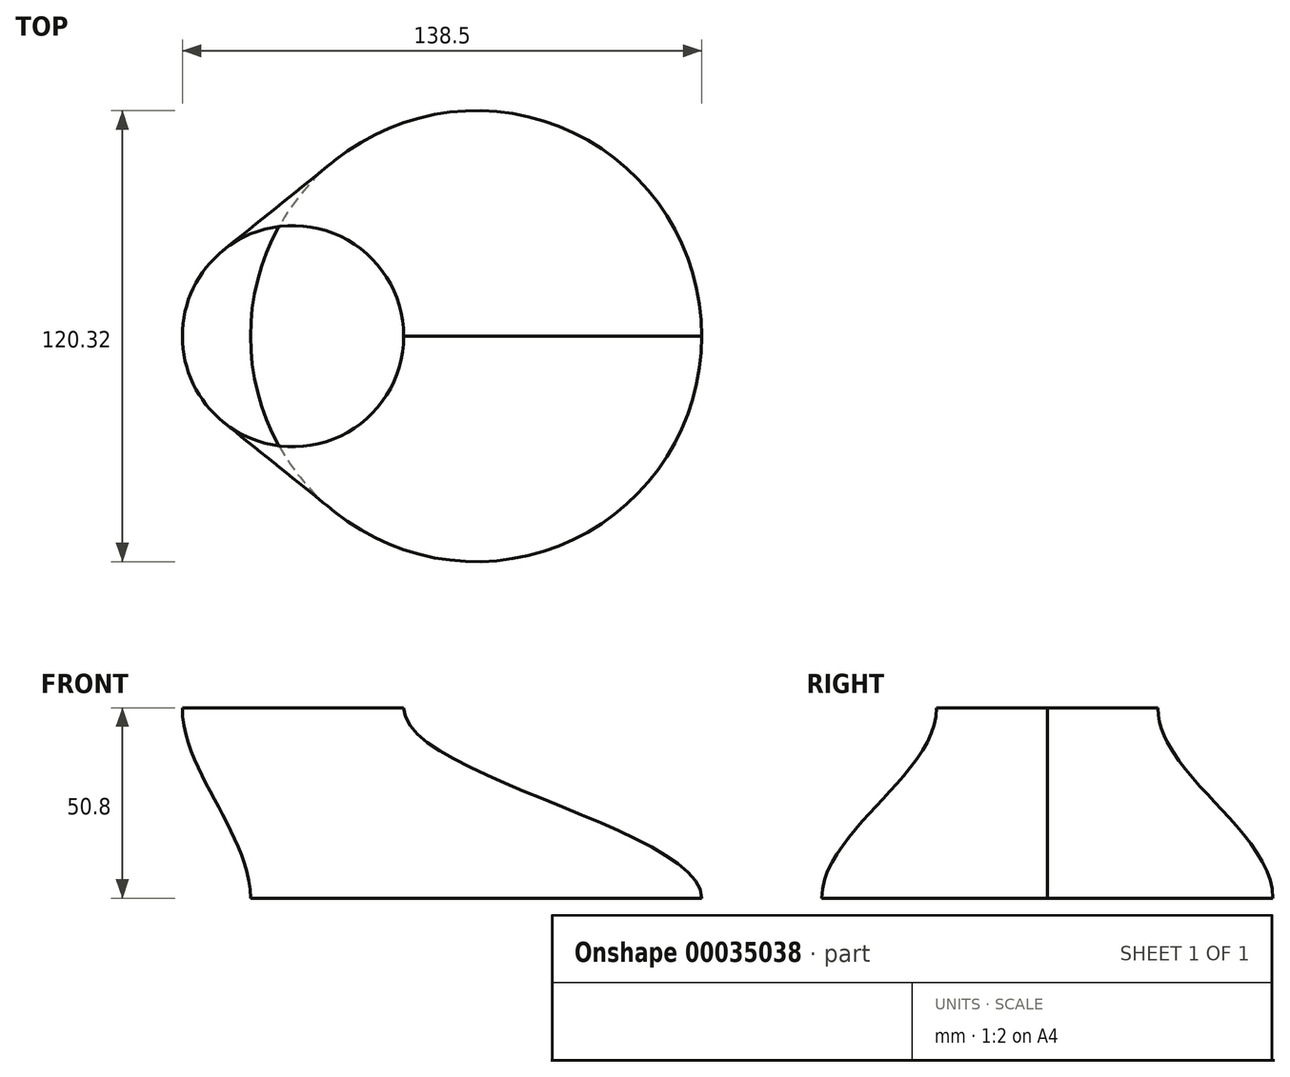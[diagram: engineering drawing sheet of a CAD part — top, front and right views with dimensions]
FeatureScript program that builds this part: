
annotation { "Feature Type Name" : "Feature", "Feature Type Description" : "" }
export const myFeature = defineFeature(function(context is Context, id is Id, definition is map)
    precondition{}
    {
        {
            var Q0;
            Q0=qCreatedBy(makeId("Top.planeOp"),FACE);
            var sketch = newSketch(context, id + "F0", { "sketchPlane" : qUnion([Q0])});
            skCircle(sketch, "E0", {"center": v(0, 0) * mm, "radius": 60.16 * mm});
            skSolve(sketch);
        }
        {
            var Q0;
            Q0=qCreatedBy(makeId("Top.planeOp"),FACE);
            cPlane(context, id + "F1", {"entities" : qUnion([Q0]), "cplaneType" : CPlaneType.OFFSET, "offset" : 50.8 * mm, "width" : 152.4 * mm, "height" : 152.4 * mm});
        }
        {
            var Q0;
            Q0=qCreatedBy(id+"F1.planeOp",FACE);
            var sketch = newSketch(context, id + "F2", { "sketchPlane" : qUnion([Q0])});
            skCircle(sketch, "E1", {"center": v(-48.83, 0) * mm, "radius": 29.5 * mm});
            skSolve(sketch);
        }
        {
            var Q0;
            Q0 = qConstructionFilter(qBodyType(qCreatedBy(id + "F0" ,EDGE), BodyType.WIRE), ConstructionObject.NO);
            var Q1;
            Q1 = qConstructionFilter(qBodyType(qCreatedBy(id + "F2" ,EDGE), BodyType.WIRE), ConstructionObject.NO);
            loft(context, id + "F3", {"bodyType" : ToolBodyType.SURFACE, "startCondition" : LoftEndDerivativeType.NORMAL_TO_PROFILE, "startMagnitude" : 1, "endCondition" : LoftEndDerivativeType.NORMAL_TO_PROFILE, "endMagnitude" : 1, "wireProfilesArray" : [{ "wireProfileEntities" : qUnion([Q0]) }, { "wireProfileEntities" : qUnion([Q1]) }]});
        }
    });
